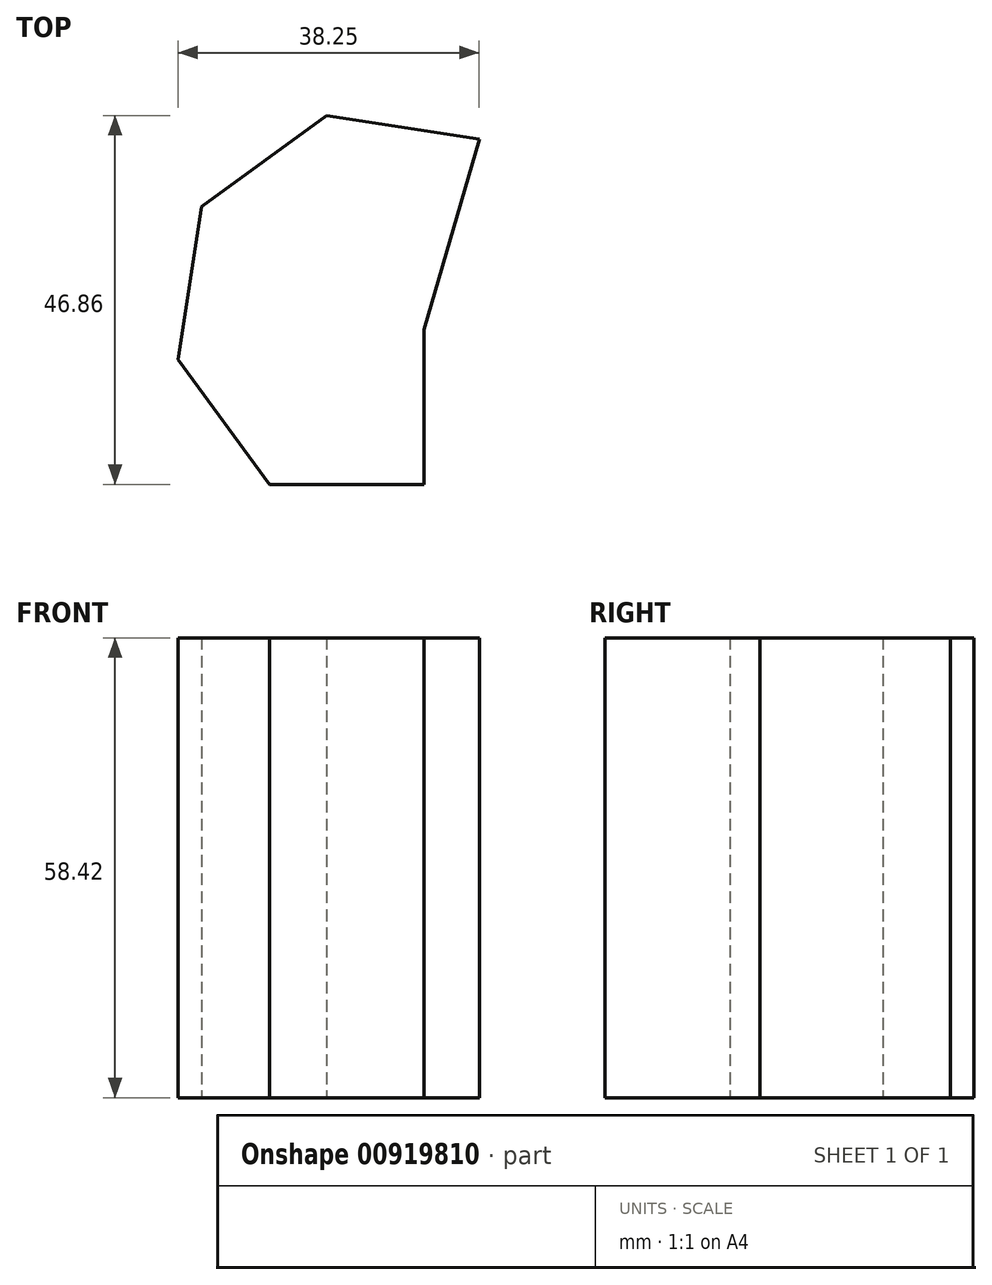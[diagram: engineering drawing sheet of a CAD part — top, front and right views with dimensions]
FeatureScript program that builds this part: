
annotation { "Feature Type Name" : "Feature", "Feature Type Description" : "" }
export const myFeature = defineFeature(function(context is Context, id is Id, definition is map)
    precondition{}
    {
        {
            var Q0;
            Q0=qCreatedBy(makeId("Top.planeOp"),FACE);
            var sketch = newSketch(context, id + "F0", { "sketchPlane" : qUnion([Q0])});
            skLineSegment(sketch, "E0.0", {"start": v(-32.88, 60.32) * mm, "end": v(-39.89, 36.1) * mm});
            skLineSegment(sketch, "E0.2", {"start": v(-39.89, 36.1) * mm, "end": v(-39.89, 16.46) * mm});
            skLineSegment(sketch, "E0.3", {"start": v(-39.89, 16.46) * mm, "end": v(-59.53, 16.46) * mm});
            skLineSegment(sketch, "E0.4", {"start": v(-59.53, 16.46) * mm, "end": v(-71.13, 32.3) * mm});
            skLineSegment(sketch, "E0.5", {"start": v(-71.13, 32.3) * mm, "end": v(-68.13, 51.71) * mm});
            skLineSegment(sketch, "E0.6", {"start": v(-68.13, 51.71) * mm, "end": v(-52.29, 63.32) * mm});
            skLineSegment(sketch, "E0.7", {"start": v(-52.29, 63.32) * mm, "end": v(-32.88, 60.32) * mm});
            skPoint(sketch, "E0.0.midPoint", {"position": v(-36.38, 48.2) * mm});
            skSolve(sketch);
        }
        {
            var Q0;
            Q0 = qSketchRegion(id + "F0", true);
            extrude(context, id + "F1", {"entities" : qUnion([Q0]), "depth" : 58.42 * mm, "offsetDistance" : 25.4 * mm});
        }
    });
